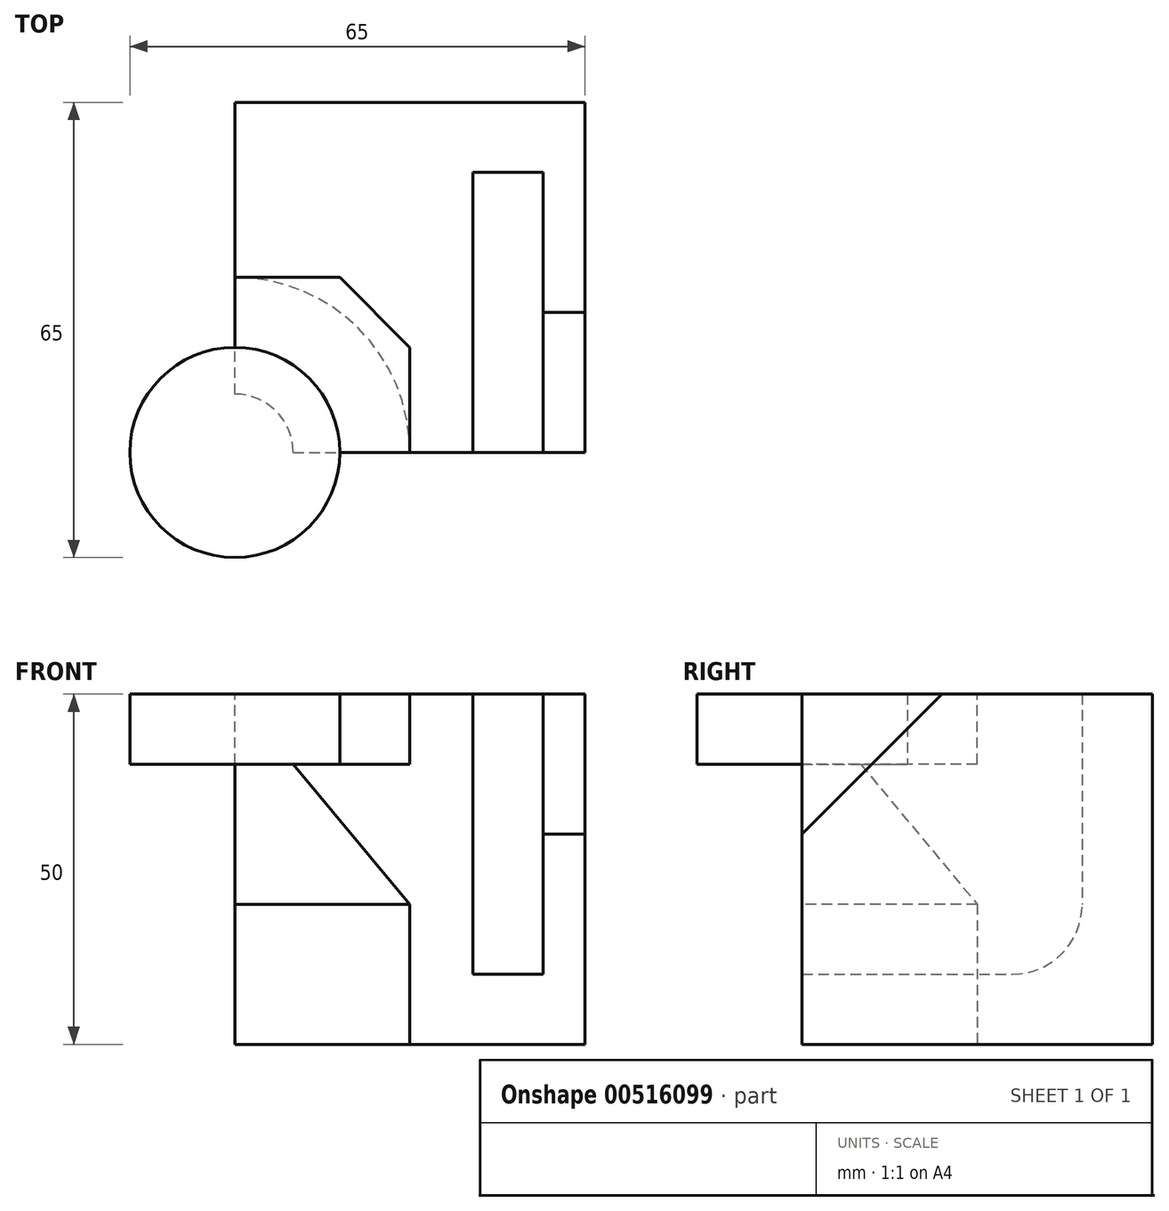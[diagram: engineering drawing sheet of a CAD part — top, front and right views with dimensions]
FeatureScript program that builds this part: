
annotation { "Feature Type Name" : "Feature", "Feature Type Description" : "" }
export const myFeature = defineFeature(function(context is Context, id is Id, definition is map)
    precondition{}
    {
        {
            var Q0;
            Q0=qCreatedBy(makeId("Top.planeOp"),FACE);
            var sketch = newSketch(context, id + "F0", { "sketchPlane" : qUnion([Q0])});
            skLineSegment(sketch, "E0.bottom", {"start": v(0, 0) * mm, "end": v(50, 0) * mm});
            skLineSegment(sketch, "E0.top", {"start": v(0, 50) * mm, "end": v(50, 50) * mm});
            skLineSegment(sketch, "E0.left", {"start": v(0, 0) * mm, "end": v(0, 50) * mm});
            skLineSegment(sketch, "E0.right", {"start": v(50, 0) * mm, "end": v(50, 50) * mm});
            skSolve(sketch);
        }
        {
            var Q0;
            Q0=makeQuery(id+"F0.imprint","IMPRINT",FACE,{"disambiguationData":[TD([[makeQuery(id+"F0.imprint","IMPRINT",EDGE,{"derivedFrom":sQuery(id+"F0.wireOp",EDGE,"E0.bottom")}),1.0]])]});
            extrude(context, id + "F1", {"entities" : qUnion([Q0]), "depth" : 50 * mm, "offsetDistance" : 25 * mm});
        }
        {
            var Q0;
            Q0=makeQuery(id+"F1.opExtrude","CAP_FACE",FACE,{"disambiguationData":[OSD([sQuery(id+"F0.wireOp",EDGE,"E0.bottom"),sQuery(id+"F0.wireOp",EDGE,"E0.top"),sQuery(id+"F0.wireOp",EDGE,"E0.left"),sQuery(id+"F0.wireOp",EDGE,"E0.right")])],"isStart":false});
            var sketch = newSketch(context, id + "F2", { "sketchPlane" : qUnion([Q0])});
            skLineSegment(sketch, "E1.bottom", {"start": v(0, 0) * mm, "end": v(25, 0) * mm});
            skLineSegment(sketch, "E1.top", {"start": v(0, 25) * mm, "end": v(25, 25) * mm});
            skLineSegment(sketch, "E1.left", {"start": v(0, 0) * mm, "end": v(0, 25) * mm});
            skLineSegment(sketch, "E1.right", {"start": v(25, 0) * mm, "end": v(25, 25) * mm});
            skSolve(sketch);
        }
        {
            var Q0;
            Q0=makeQuery(id+"F2.imprint","IMPRINT",FACE,{"disambiguationData":[TD([[makeQuery(id+"F2.imprint","IMPRINT",EDGE,{"derivedFrom":sQuery(id+"F2.wireOp",EDGE,"E1.bottom")}),1.0]])]});
            extrude(context, id + "F3", {"entities" : qUnion([Q0]), "operationType" : NewBodyOperationType.REMOVE, "oppositeDirection" : true, "depth" : 10 * mm, "offsetDistance" : 25 * mm});
        }
        {
            var Q0;
            Q0=makeQuery(id+"F3.boolean.opBoolean","COPY",FACE,{"derivedFrom":makeQuery(id+"F3.opExtrude","CAP_FACE",FACE,{"disambiguationData":[OSD([sQuery(id+"F2.wireOp",EDGE,"E1.bottom"),sQuery(id+"F2.wireOp",EDGE,"E1.top"),sQuery(id+"F2.wireOp",EDGE,"E1.left"),sQuery(id+"F2.wireOp",EDGE,"E1.right")])],"isStart":false})});
            var sketch = newSketch(context, id + "F4", { "sketchPlane" : qUnion([Q0])});
            skLineSegment(sketch, "E2", {"start": v(15, 25) * mm, "end": v(25, 15) * mm});
            skSolve(sketch);
        }
        {
            var Q0;
            {var subQ0=sQuery(id+"F4.wireOp",EDGE,"E2");Q0=makeQuery(id+"F4.imprint","IMPRINT",FACE,{"disambiguationData":[TD([[makeQuery(id+"F4.imprint","IMPRINT",EDGE,{"derivedFrom":subQ0}),1.0]])]});}
            extrude(context, id + "F5", {"entities" : qUnion([Q0]), "operationType" : NewBodyOperationType.ADD, "depth" : 10 * mm, "offsetDistance" : 25 * mm});
        }
        {
            var Q0;
            Q0=makeQuery(id+"F3.boolean.opBoolean","COPY",FACE,{"derivedFrom":makeQuery(id+"F3.opExtrude","CAP_FACE",FACE,{"disambiguationData":[OSD([sQuery(id+"F2.wireOp",EDGE,"E1.bottom"),sQuery(id+"F2.wireOp",EDGE,"E1.top"),sQuery(id+"F2.wireOp",EDGE,"E1.left"),sQuery(id+"F2.wireOp",EDGE,"E1.right")])],"isStart":false})});
            var sketch = newSketch(context, id + "F6", { "sketchPlane" : qUnion([Q0])});
            skCircle(sketch, "E3", {"center": v(0, 0) * mm, "radius": 15 * mm});
            skSolve(sketch);
        }
        {
            var Q0;
            {var subQ0=sQuery(id+"F6.wireOp",EDGE,"E3");var subQ1=makeQuery(id+"F3.boolean.opBoolean","COPY",EDGE,{"derivedFrom":makeQuery(id+"F3.opExtrude","CAP_EDGE",EDGE,{"disambiguationData":[OSD([sQuery(id+"F2.wireOp",EDGE,"E1.bottom")])],"isStart":false})});var subQ2=makeQuery(id+"F6.imprint","INTERSECT",VERTEX,{"derivedFrom":[subQ1,subQ0]});Q0=makeQuery(id+"F6.imprint","IMPRINT",FACE,{"disambiguationData":[TD([[makeQuery(id+"F6.imprint","IMPRINT",EDGE,{"disambiguationData":[TD([[subQ2,-1.0]])],"derivedFrom":subQ0}),1.0]])]});}
            extrude(context, id + "F7", {"entities" : qUnion([Q0]), "operationType" : NewBodyOperationType.ADD, "depth" : 10 * mm, "offsetDistance" : 25 * mm});
        }
        {
            var Q0;
            Q0=makeQuery(id+"F1.opExtrude","CAP_FACE",FACE,{"disambiguationData":[OSD([sQuery(id+"F0.wireOp",EDGE,"E0.bottom"),sQuery(id+"F0.wireOp",EDGE,"E0.top"),sQuery(id+"F0.wireOp",EDGE,"E0.left"),sQuery(id+"F0.wireOp",EDGE,"E0.right")])],"isStart":true});
            var sketch = newSketch(context, id + "F8", { "sketchPlane" : qUnion([Q0])});
            skCircle(sketch, "E4", {"center": v(0, 0) * mm, "radius": 25 * mm});
            skSolve(sketch);
        }
        {
            var Q0;
            Q0 = qSketchRegion(id + "F8", true);
            extrude(context, id + "F9", {"entities" : qUnion([Q0]), "operationType" : NewBodyOperationType.REMOVE, "oppositeDirection" : true, "depth" : 20 * mm, "offsetDistance" : 25 * mm});
        }
        {
            var Q0;
            Q0=makeQuery(id+"F7.boolean.opBoolean","MERGE",FACE,{"derivedFrom":[makeQuery(id+"F1.opExtrude","SWEPT_FACE",FACE,{"disambiguationData":[OSD([sQuery(id+"F0.wireOp",EDGE,"E0.bottom")])]}),makeQuery(id+"F7.opExtrude","SWEPT_FACE",FACE,{"disambiguationData":[OSD([sQuery(id+"F2.wireOp",EDGE,"E1.bottom")])]})]});
            var sketch = newSketch(context, id + "F10", { "sketchPlane" : qUnion([Q0])});
            skLineSegment(sketch, "E5", {"start": v(0, 50) * mm, "end": v(25, 20) * mm});
            skSolve(sketch);
        }
        {
            var Q0;
            Q0=makeQuery(id+"F10.imprint","IMPRINT",FACE,{"disambiguationData":[TD([[makeQuery(id+"F10.imprint","IMPRINT",EDGE,{"derivedFrom":sQuery(id+"F10.wireOp",EDGE,"E5")}),-1.0]])]});
            var Q1;
            Q1=makeQuery(id+"F9.boolean.opBoolean","COPY",FACE,{"derivedFrom":makeQuery(id+"F9.opExtrude","SWEPT_FACE",FACE,{"disambiguationData":[OSD([sQuery(id+"F8.wireOp",EDGE,"E4")])]})});
            revolve(context, id + "F11", {"operationType" : NewBodyOperationType.REMOVE, "entities" : qUnion([Q0]), "axis" : qUnion([Q1]), "revolveType" : RevolveType.FULL, "oppositeDirection" : true});
        }
        {
            var Q0;
            Q0=makeQuery(id+"F5.boolean.opBoolean","MERGE",FACE,{"derivedFrom":[makeQuery(id+"F1.opExtrude","CAP_FACE",FACE,{"disambiguationData":[OSD([sQuery(id+"F0.wireOp",EDGE,"E0.bottom"),sQuery(id+"F0.wireOp",EDGE,"E0.top"),sQuery(id+"F0.wireOp",EDGE,"E0.left"),sQuery(id+"F0.wireOp",EDGE,"E0.right")])],"isStart":false}),makeQuery(id+"F5.opExtrude","CAP_FACE",FACE,{"disambiguationData":[OSD([sQuery(id+"F2.wireOp",EDGE,"E1.top"),sQuery(id+"F2.wireOp",EDGE,"E1.right"),sQuery(id+"F4.wireOp",EDGE,"E2")])],"isStart":false})]});
            var sketch = newSketch(context, id + "F12", { "sketchPlane" : qUnion([Q0])});
            skLineSegment(sketch, "E6.bottom", {"start": v(34, 0) * mm, "end": v(44, 0) * mm});
            skLineSegment(sketch, "E6.top", {"start": v(34, 40) * mm, "end": v(44, 40) * mm});
            skLineSegment(sketch, "E6.left", {"start": v(34, 0) * mm, "end": v(34, 40) * mm});
            skLineSegment(sketch, "E6.right", {"start": v(44, 0) * mm, "end": v(44, 40) * mm});
            skSolve(sketch);
        }
        {
            var Q0;
            Q0=makeQuery(id+"F1.opExtrude","SWEPT_FACE",FACE,{"disambiguationData":[OSD([sQuery(id+"F0.wireOp",EDGE,"E0.right")])]});
            var sketch = newSketch(context, id + "F13", { "sketchPlane" : qUnion([Q0])});
            skLineSegment(sketch, "E7.bottom", {"start": v(40, 50) * mm, "end": v(0, 50) * mm});
            skLineSegment(sketch, "E7.top", {"start": v(40, 10) * mm, "end": v(0, 10) * mm});
            skLineSegment(sketch, "E7.left", {"start": v(40, 50) * mm, "end": v(40, 10) * mm});
            skLineSegment(sketch, "E7.right", {"start": v(0, 50) * mm, "end": v(0, 10) * mm});
            skPoint(sketch, "E8.visualSharp", {"position": v(40, 10) * mm});
            skLineSegment(sketch, "E8.filletArc", {"start": v(40, 10) * mm, "end": v(40, 10) * mm});
            skSolve(sketch);
        }
        {
            var Q0;
            Q0=makeQuery(id+"F12.imprint","IMPRINT",FACE,{"disambiguationData":[TD([[makeQuery(id+"F12.imprint","IMPRINT",EDGE,{"derivedFrom":sQuery(id+"F12.wireOp",EDGE,"E6.bottom")}),1.0]])]});
            var Q1;
            Q1=sQuery(id+"F13.wireOp",EDGE,"E7.left");
            sweep(context, id + "F14", {"operationType" : NewBodyOperationType.REMOVE, "profiles" : qUnion([Q0]), "path" : qUnion([Q1])});
        }
        {
            var Q0;
            Q0=makeQuery(id+"F14.boolean.opBoolean","COPY",EDGE,{"derivedFrom":makeQuery(id+"F14.opSweep","CAP_EDGE",EDGE,{"disambiguationData":[OSD([sQuery(id+"F12.wireOp",EDGE,"E6.top"),sQuery(id+"F13.wireOp",VERTEX,"E7.left.end")])],"isStart":false})});
            fillet(context, id + "F15", {"entities" : qUnion([Q0]), "radius" : 10 * mm, "tangentPropagation" : true, "allowEdgeOverflow" : false});
        }
        {
            var Q0;
            Q0=makeQuery(id+"F1.opExtrude","SWEPT_FACE",FACE,{"disambiguationData":[OSD([sQuery(id+"F0.wireOp",EDGE,"E0.right")])]});
            var sketch = newSketch(context, id + "F16", { "sketchPlane" : qUnion([Q0])});
            skLineSegment(sketch, "E9", {"start": v(0, 30) * mm, "end": v(20, 50) * mm});
            skSolve(sketch);
        }
        {
            var Q0;
            {var subQ0=sQuery(id+"F16.wireOp",EDGE,"E9");Q0=makeQuery(id+"F16.imprint","IMPRINT",FACE,{"disambiguationData":[TD([[makeQuery(id+"F16.imprint","IMPRINT",EDGE,{"derivedFrom":subQ0}),1.0]])]});}
            extrude(context, id + "F17", {"entities" : qUnion([Q0]), "operationType" : NewBodyOperationType.REMOVE, "endBound" : BoundingType.UP_TO_NEXT, "oppositeDirection" : true, "depth" : 25 * mm, "offsetDistance" : 25 * mm});
        }
    });
